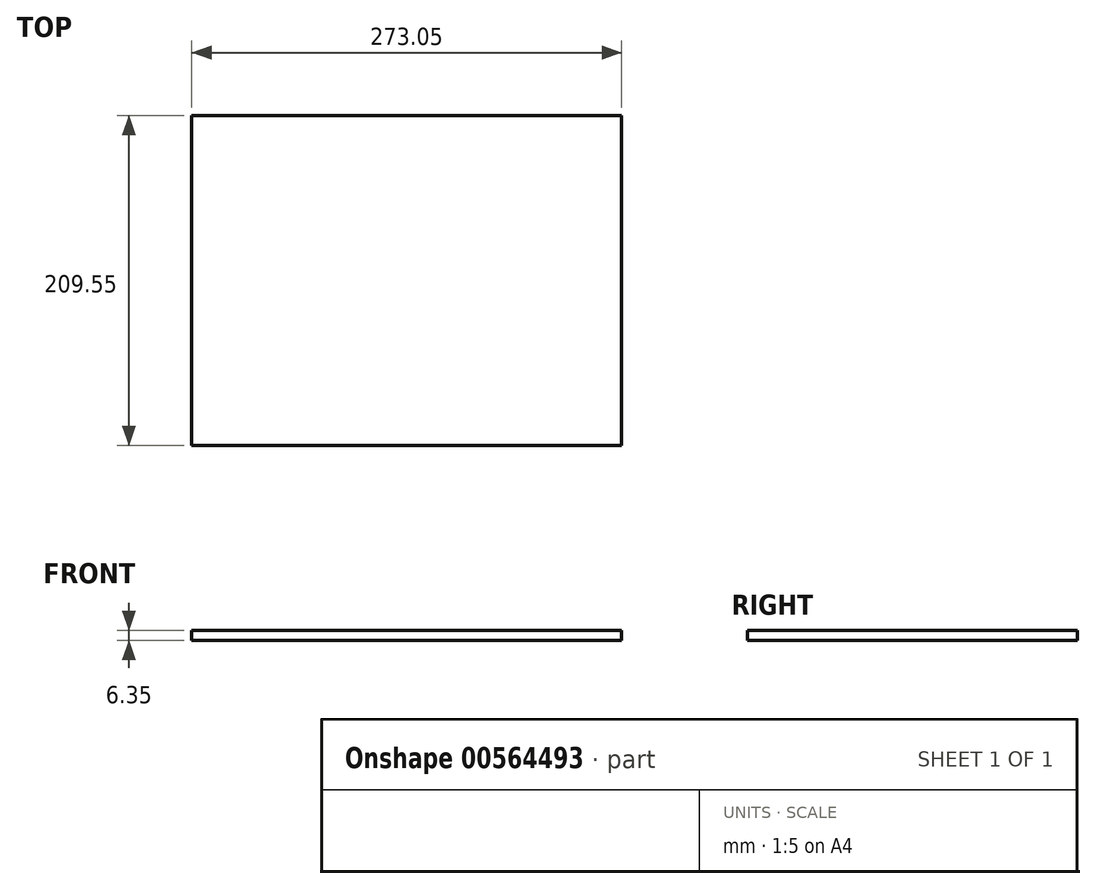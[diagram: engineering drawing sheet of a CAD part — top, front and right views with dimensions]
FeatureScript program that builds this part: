
annotation { "Feature Type Name" : "Feature", "Feature Type Description" : "" }
export const myFeature = defineFeature(function(context is Context, id is Id, definition is map)
    precondition{}
    {
        {
            var Q0;
            Q0=qCreatedBy(makeId("Top.planeOp"),FACE);
            var sketch = newSketch(context, id + "F0", { "sketchPlane" : qUnion([Q0])});
            skLineSegment(sketch, "E0.bottom", {"start": v(0, 0) * mm, "end": v(273.05, 0) * mm});
            skLineSegment(sketch, "E0.top", {"start": v(0, -209.55) * mm, "end": v(273.05, -209.55) * mm});
            skLineSegment(sketch, "E0.left", {"start": v(0, 0) * mm, "end": v(0, -209.55) * mm});
            skLineSegment(sketch, "E0.right", {"start": v(273.05, 0) * mm, "end": v(273.05, -209.55) * mm});
            skSolve(sketch);
        }
        {
            var Q0;
            Q0=makeQuery(id+"F0.imprint","IMPRINT",FACE,{"disambiguationData":[TD([[makeQuery(id+"F0.imprint","IMPRINT",EDGE,{"derivedFrom":sQuery(id+"F0.wireOp",EDGE,"E0.bottom")}),-1.0]])]});
            extrude(context, id + "F1", {"entities" : qUnion([Q0]), "depth" : 6.35 * mm, "offsetDistance" : 25.4 * mm});
        }
    });
